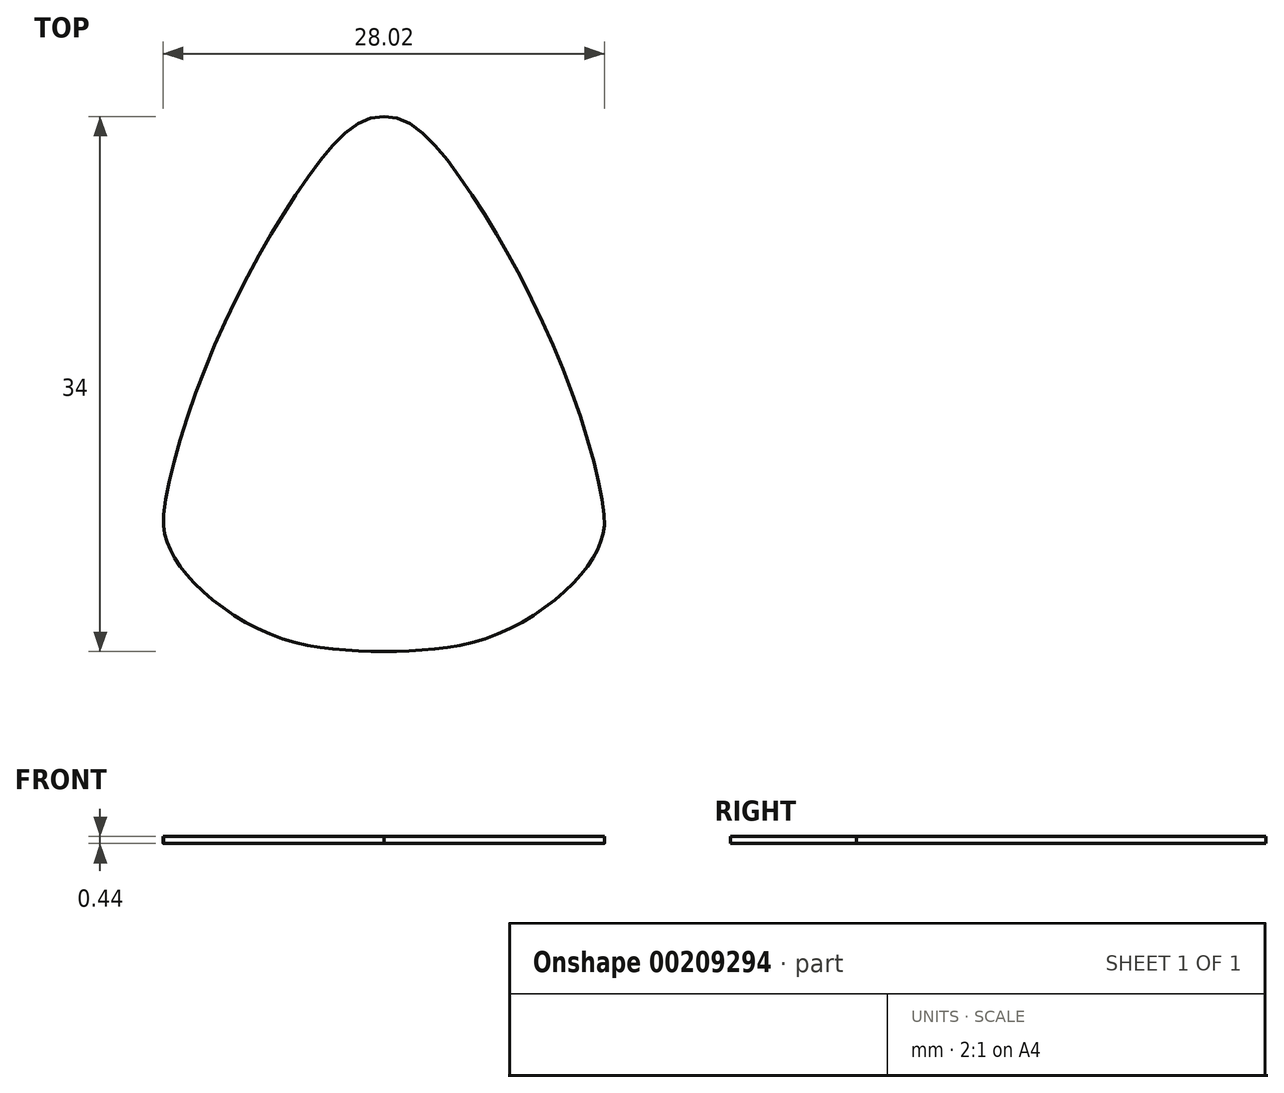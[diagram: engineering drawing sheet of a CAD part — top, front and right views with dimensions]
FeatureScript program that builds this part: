
annotation { "Feature Type Name" : "Feature", "Feature Type Description" : "" }
export const myFeature = defineFeature(function(context is Context, id is Id, definition is map)
    precondition{}
    {
        {
            var Q0;
            Q0=qCreatedBy(makeId("Top.planeOp"),FACE);
            var sketch = newSketch(context, id + "F0", { "sketchPlane" : qUnion([Q0])});
            skLineSegment(sketch, "E0", {"start": v(0, 0) * mm, "end": v(14, 0) * mm, "construction": true});
            skLineSegment(sketch, "E1", {"start": v(0, 0) * mm, "end": v(0, 26) * mm});
            skLineSegment(sketch, "E2", {"start": v(0, 0) * mm, "end": v(0, -8) * mm});
            skPoint(sketch, "E3.visualSharp", {"position": v(0, 26) * mm});
            skPoint(sketch, "E4.visualSharp", {"position": v(14, 0) * mm});
            skPoint(sketch, "E5.visualSharp", {"position": v(-14, 0) * mm});
            skPoint(sketch, "E6.visualSharp", {"position": v(0, -8) * mm});
            skFitSpline(sketch, "E7", {"points": [v(14, 0) * mm, v(11.62, 9.32) * mm, v(4.96, 21.93) * mm, v(0, 26) * mm], "startDerivative": vector(1.14, 13.58) * mm, "endDerivative": vector(-19.46, -1.2) * mm});
            skFitSpline(sketch, "E8", {"points": [v(0, -8) * mm, v(6.82, -7.05) * mm, v(12.52, -3.11) * mm, v(14, 0) * mm], "startDerivative": vector(18.55, 0.5) * mm, "endDerivative": vector(1.4, 11.8) * mm});
            skSolve(sketch);
        }
        {
            var Q0;
            Q0=makeQuery(id+"F0.imprint","IMPRINT",FACE,{"disambiguationData":[TD([[makeQuery(id+"F0.imprint","IMPRINT",EDGE,{"derivedFrom":sQuery(id+"F0.wireOp",EDGE,"E1")}),-1.0]])]});
            extrude(context, id + "F1", {"entities" : qUnion([Q0]), "depth" : .44 * mm});
        }
        {
            var Q0;
            Q0=makeQuery(id+"F1.opExtrude","SWEPT_BODY",BODY,{"disambiguationData":[OSD([sQuery(id+"F0.wireOp",EDGE,"E1"),sQuery(id+"F0.wireOp",EDGE,"E2"),sQuery(id+"F0.wireOp",EDGE,"E7"),sQuery(id+"F0.wireOp",EDGE,"E8")])]});
            var Q1;
            Q1=qCreatedBy(makeId("Right.planeOp"),FACE);
            mirror(context, id + "F2", {"operationType" : NewBodyOperationType.ADD, "entities" : qUnion([Q0]), "mirrorPlane" : qUnion([Q1])});
        }
    });
